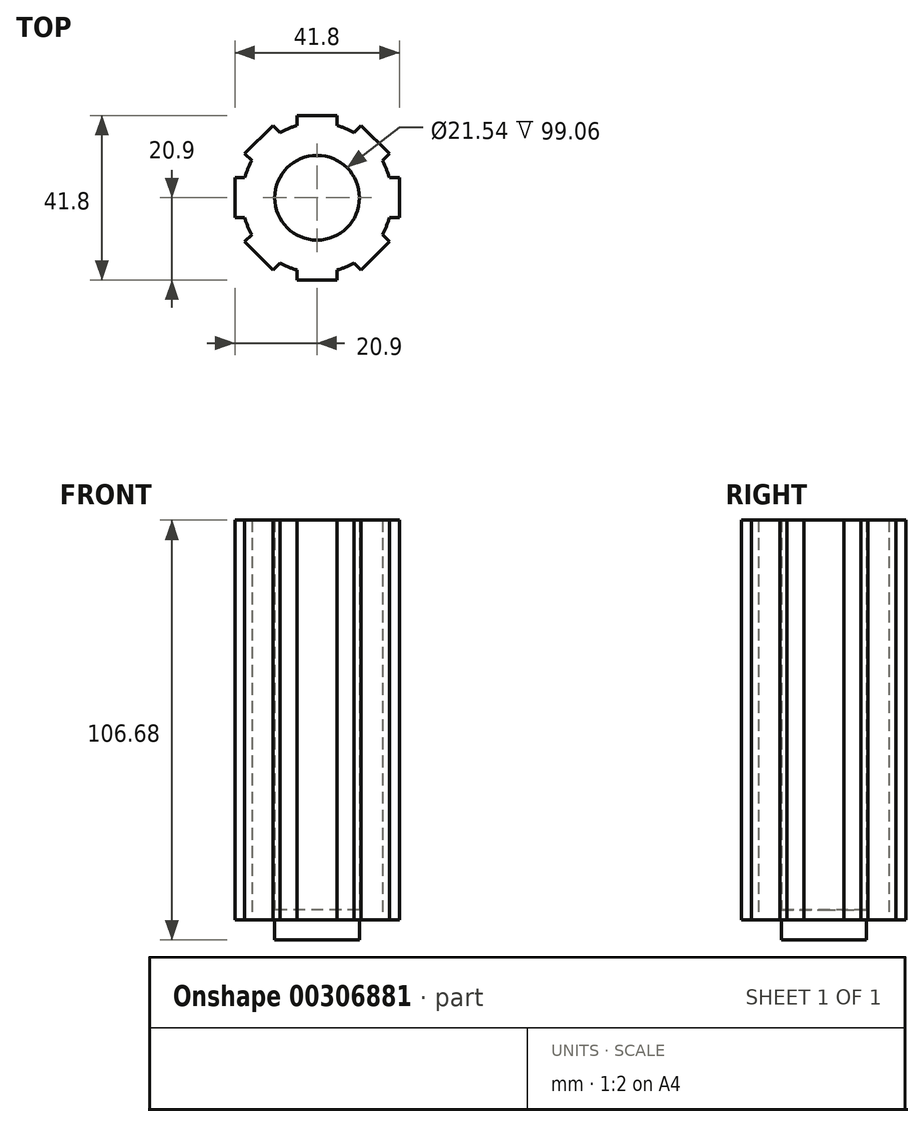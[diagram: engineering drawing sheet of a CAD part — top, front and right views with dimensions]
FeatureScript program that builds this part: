
annotation { "Feature Type Name" : "Feature", "Feature Type Description" : "" }
export const myFeature = defineFeature(function(context is Context, id is Id, definition is map)
    precondition{}
    {
        {
            var Q0;
            Q0=qCreatedBy(makeId("Top.planeOp"),FACE);
            var sketch = newSketch(context, id + "F0", { "sketchPlane" : qUnion([Q0])});
            skCircle(sketch, "E0", {"center": v(0, 0) * mm, "radius": 19.05 * mm, "construction": true});
            skLineSegment(sketch, "E1.top", {"start": v(-5.08, 20.9) * mm, "end": v(5.08, 20.9) * mm});
            skLineSegment(sketch, "E1.left", {"start": v(-5.08, 18.36) * mm, "end": v(-5.08, 20.9) * mm});
            skLineSegment(sketch, "E1.right", {"start": v(5.08, 18.36) * mm, "end": v(5.08, 20.9) * mm});
            skLineSegment(sketch, "E2.bottom", {"start": v(-18.36, -5.08) * mm, "end": v(-20.9, -5.08) * mm});
            skLineSegment(sketch, "E2.top", {"start": v(-18.36, 5.08) * mm, "end": v(-20.9, 5.08) * mm});
            skLineSegment(sketch, "E2.right", {"start": v(-20.9, -5.08) * mm, "end": v(-20.9, 5.08) * mm});
            skLineSegment(sketch, "E3.top", {"start": v(-5.08, -20.9) * mm, "end": v(5.08, -20.9) * mm});
            skLineSegment(sketch, "E3.left", {"start": v(-5.08, -18.36) * mm, "end": v(-5.08, -20.9) * mm});
            skLineSegment(sketch, "E3.right", {"start": v(5.08, -18.36) * mm, "end": v(5.08, -20.9) * mm});
            skLineSegment(sketch, "E4", {"start": v(9.4, 16.57) * mm, "end": v(11.19, 18.37) * mm});
            skLineSegment(sketch, "E5", {"start": v(11.19, 18.37) * mm, "end": v(18.37, 11.19) * mm});
            skLineSegment(sketch, "E6", {"start": v(18.37, 11.19) * mm, "end": v(16.57, 9.4) * mm});
            skLineSegment(sketch, "E7", {"start": v(18.36, -5.08) * mm, "end": v(20.9, -5.08) * mm});
            skLineSegment(sketch, "E8", {"start": v(20.9, -5.08) * mm, "end": v(20.9, 5.08) * mm});
            skLineSegment(sketch, "E9", {"start": v(20.9, 5.08) * mm, "end": v(18.36, 5.08) * mm});
            skLineSegment(sketch, "E10", {"start": v(9.4, -16.57) * mm, "end": v(11.19, -18.37) * mm});
            skLineSegment(sketch, "E11", {"start": v(11.19, -18.37) * mm, "end": v(18.37, -11.19) * mm});
            skLineSegment(sketch, "E12", {"start": v(18.37, -11.19) * mm, "end": v(16.57, -9.4) * mm});
            skCircle(sketch, "E13", {"center": v(0, 0) * mm, "radius": 10.77 * mm});
            skLineSegment(sketch, "E14", {"start": v(-16.57, -9.4) * mm, "end": v(-18.37, -11.19) * mm});
            skLineSegment(sketch, "E15", {"start": v(-18.37, -11.19) * mm, "end": v(-11.19, -18.37) * mm});
            skLineSegment(sketch, "E16", {"start": v(-11.19, -18.37) * mm, "end": v(-9.4, -16.57) * mm});
            skLineSegment(sketch, "E17", {"start": v(-16.57, 9.4) * mm, "end": v(-18.37, 11.19) * mm});
            skLineSegment(sketch, "E18", {"start": v(-18.37, 11.19) * mm, "end": v(-11.19, 18.37) * mm});
            skLineSegment(sketch, "E19", {"start": v(-11.19, 18.37) * mm, "end": v(-9.4, 16.57) * mm});
            skLineSegment(sketch, "E20", {"start": v(-11.19, 18.37) * mm, "end": v(-5.08, 20.9) * mm, "construction": true});
            skLineSegment(sketch, "E21", {"start": v(5.08, 20.9) * mm, "end": v(11.19, 18.37) * mm, "construction": true});
            skLineSegment(sketch, "E22", {"start": v(18.37, 11.19) * mm, "end": v(20.9, 5.08) * mm, "construction": true});
            skLineSegment(sketch, "E23", {"start": v(20.9, -5.08) * mm, "end": v(18.37, -11.19) * mm, "construction": true});
            skLineSegment(sketch, "E24", {"start": v(11.19, -18.37) * mm, "end": v(5.08, -20.9) * mm, "construction": true});
            skLineSegment(sketch, "E25", {"start": v(-5.08, -20.9) * mm, "end": v(-11.19, -18.37) * mm, "construction": true});
            skLineSegment(sketch, "E26", {"start": v(-18.37, -11.19) * mm, "end": v(-20.9, -5.08) * mm, "construction": true});
            skLineSegment(sketch, "E27", {"start": v(-20.9, 5.08) * mm, "end": v(-18.37, 11.19) * mm, "construction": true});
            skArc(sketch, "E28", {"start": v(-16.57, 9.4) * mm, "mid": v(-17.6, 7.3) * mm, "end": v(-18.36, 5.08) * mm});
            skArc(sketch, "E29", {"start": v(-5.08, 18.36) * mm, "mid": v(-7.3, 17.6) * mm, "end": v(-9.4, 16.57) * mm});
            skArc(sketch, "E30", {"start": v(9.4, 16.57) * mm, "mid": v(7.3, 17.6) * mm, "end": v(5.08, 18.36) * mm});
            skArc(sketch, "E31", {"start": v(18.36, 5.08) * mm, "mid": v(17.6, 7.3) * mm, "end": v(16.57, 9.4) * mm});
            skArc(sketch, "E32", {"start": v(16.57, -9.4) * mm, "mid": v(17.6, -7.3) * mm, "end": v(18.36, -5.08) * mm});
            skArc(sketch, "E33", {"start": v(5.08, -18.36) * mm, "mid": v(7.3, -17.6) * mm, "end": v(9.4, -16.57) * mm});
            skArc(sketch, "E34", {"start": v(-9.4, -16.57) * mm, "mid": v(-7.3, -17.6) * mm, "end": v(-5.08, -18.36) * mm});
            skArc(sketch, "E35", {"start": v(-18.36, -5.08) * mm, "mid": v(-17.6, -7.3) * mm, "end": v(-16.57, -9.4) * mm});
            skSolve(sketch);
        }
        {
            var Q0;
            Q0=makeQuery(id+"F0.imprint","IMPRINT",FACE,{"disambiguationData":[TD([[makeQuery(id+"F0.imprint","IMPRINT",EDGE,{"derivedFrom":sQuery(id+"F0.wireOp",EDGE,"E13")}),1.0]])]});
            extrude(context, id + "F1", {"entities" : qUnion([Q0]), "depth" : 2.54 * mm});
        }
        {
            var Q0;
            Q0=makeQuery(id+"F0.imprint","IMPRINT",FACE,{"disambiguationData":[TD([[makeQuery(id+"F0.imprint","IMPRINT",EDGE,{"derivedFrom":sQuery(id+"F0.wireOp",EDGE,"E1.top")}),-1.0]])]});
            extrude(context, id + "F2", {"entities" : qUnion([Q0]), "operationType" : NewBodyOperationType.ADD, "depth" : 101.6 * mm});
        }
        {
            var Q0;
            Q0=makeQuery(id+"F0.imprint","IMPRINT",FACE,{"disambiguationData":[TD([[makeQuery(id+"F0.imprint","IMPRINT",EDGE,{"derivedFrom":sQuery(id+"F0.wireOp",EDGE,"E13")}),1.0]])]});
            extrude(context, id + "F3", {"entities" : qUnion([Q0]), "operationType" : NewBodyOperationType.ADD, "oppositeDirection" : true, "depth" : 5.08 * mm});
        }
    });
